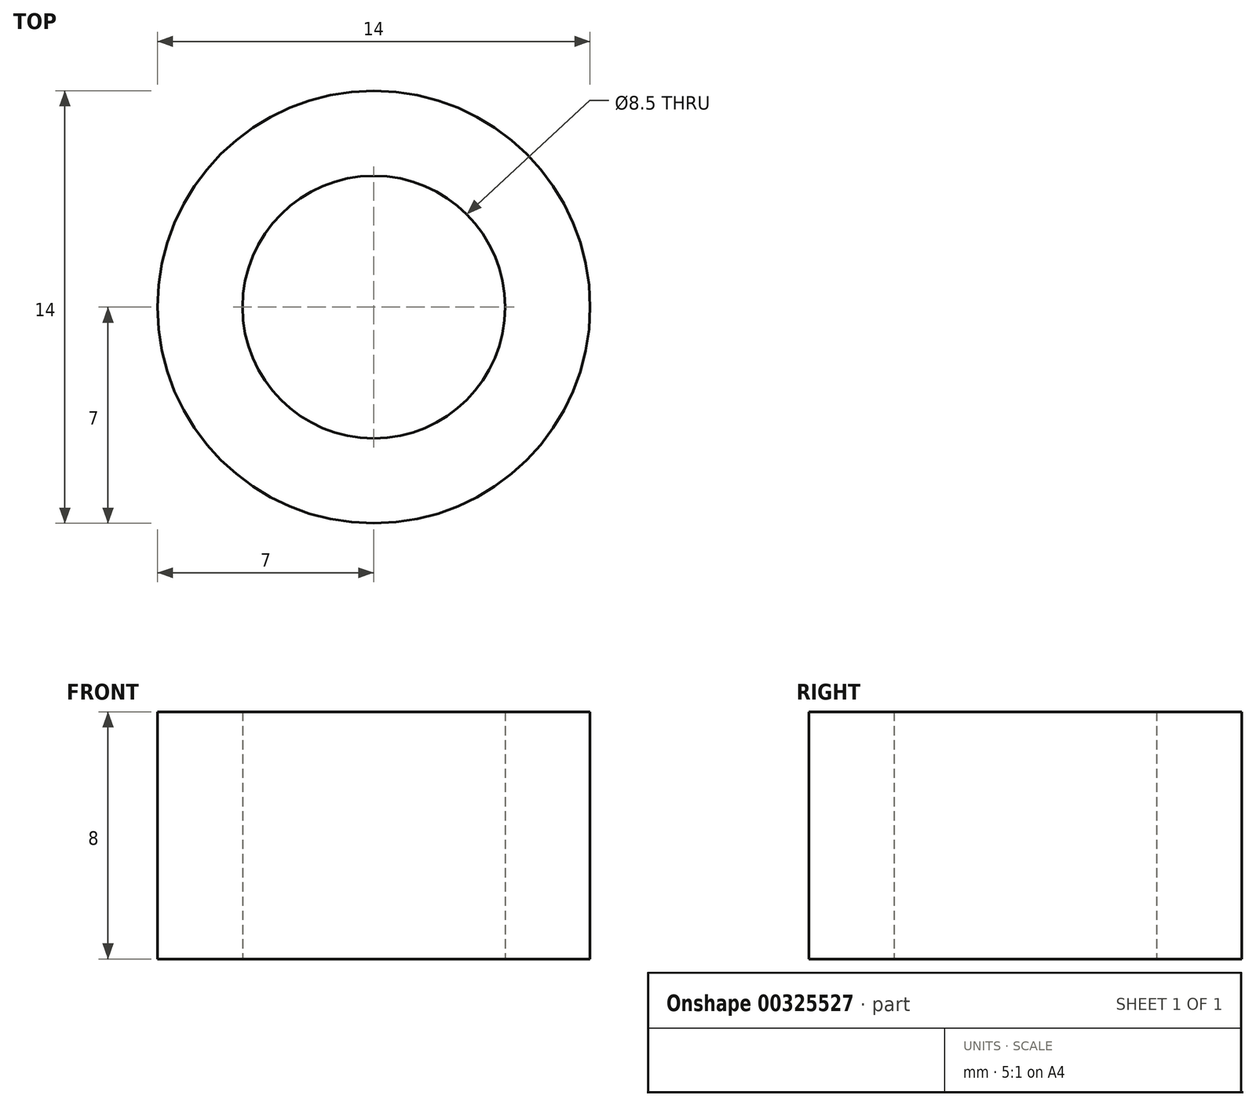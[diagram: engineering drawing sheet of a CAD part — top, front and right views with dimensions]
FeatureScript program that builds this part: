
annotation { "Feature Type Name" : "Feature", "Feature Type Description" : "" }
export const myFeature = defineFeature(function(context is Context, id is Id, definition is map)
    precondition{}
    {
        {
            var Q0;
            Q0=qCreatedBy(makeId("Top.planeOp"),FACE);
            var sketch = newSketch(context, id + "F0", { "sketchPlane" : qUnion([Q0])});
            skCircle(sketch, "E0", {"center": v(0, 0) * mm, "radius": 4.25 * mm});
            skCircle(sketch, "E1", {"center": v(0, 0) * mm, "radius": 7 * mm});
            skSolve(sketch);
        }
        {
            var Q0;
            Q0=makeQuery(id+"F0.imprint","IMPRINT",FACE,{"disambiguationData":[TD([[makeQuery(id+"F0.imprint","IMPRINT",EDGE,{"derivedFrom":sQuery(id+"F0.wireOp",EDGE,"E0")}),-1.0]])]});
            extrude(context, id + "F1", {"entities" : qUnion([Q0]), "depth" : 8 * mm});
        }
    });
